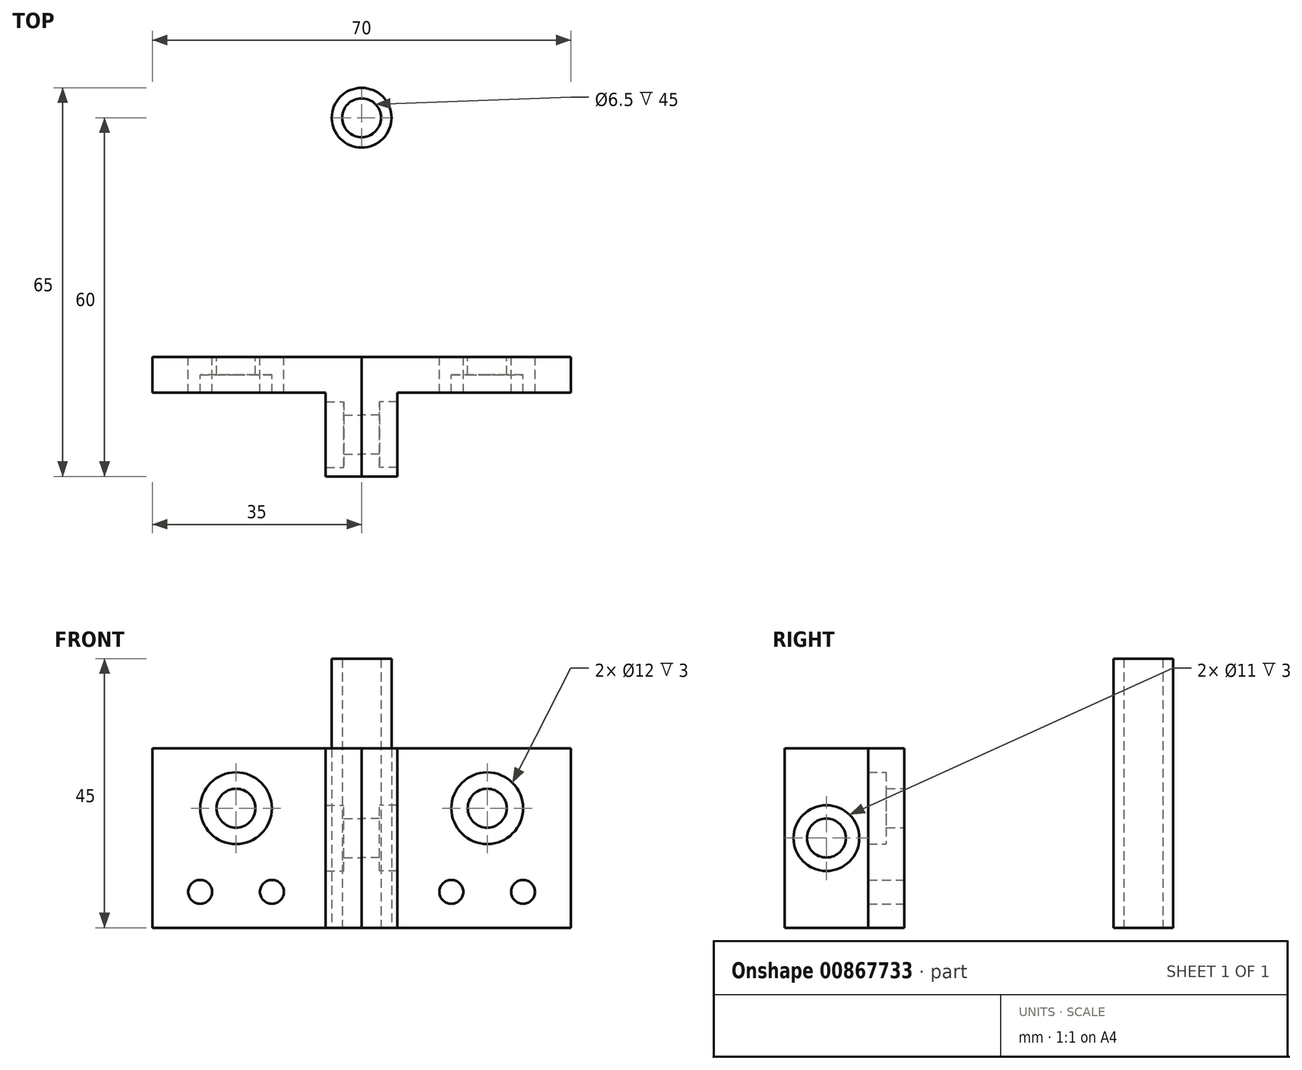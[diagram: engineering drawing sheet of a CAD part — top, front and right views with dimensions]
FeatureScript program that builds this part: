
annotation { "Feature Type Name" : "Feature", "Feature Type Description" : "" }
export const myFeature = defineFeature(function(context is Context, id is Id, definition is map)
    precondition{}
    {
        {
            var Q0;
            Q0=qCreatedBy(makeId("Top.planeOp"),FACE);
            var sketch = newSketch(context, id + "F0", { "sketchPlane" : qUnion([Q0])});
            skLineSegment(sketch, "E0", {"start": v(0, -20) * mm, "end": v(0, 0) * mm});
            skLineSegment(sketch, "E1", {"start": v(0, 0) * mm, "end": v(-35, 0) * mm});
            skLineSegment(sketch, "E2", {"start": v(-35, 0) * mm, "end": v(-35, -6) * mm});
            skLineSegment(sketch, "E3", {"start": v(-35, -6) * mm, "end": v(-6, -6) * mm});
            skLineSegment(sketch, "E4", {"start": v(-6, -6) * mm, "end": v(-6, -20) * mm});
            skLineSegment(sketch, "E5", {"start": v(-6, -20) * mm, "end": v(0, -20) * mm});
            skCircle(sketch, "E6", {"center": v(0, 40) * mm, "radius": 3.25 * mm});
            skCircle(sketch, "E7", {"center": v(0, 40) * mm, "radius": 5 * mm});
            skSolve(sketch);
        }
        {
            var Q0;
            Q0=makeQuery(id+"F0.imprint","IMPRINT",FACE,{"disambiguationData":[TD([[makeQuery(id+"F0.imprint","IMPRINT",EDGE,{"derivedFrom":sQuery(id+"F0.wireOp",EDGE,"E0")}),1.0]])]});
            extrude(context, id + "F1", {"entities" : qUnion([Q0]), "depth" : 30 * mm, "offsetDistance" : 25 * mm});
        }
        {
            var Q0;
            Q0=makeQuery(id+"F1.opExtrude","SWEPT_FACE",FACE,{"disambiguationData":[OSD([sQuery(id+"F0.wireOp",EDGE,"E3")])]});
            var sketch = newSketch(context, id + "F2", { "sketchPlane" : qUnion([Q0])});
            skLineSegment(sketch, "E8.0", {"start": v(-35, 30) * mm, "end": v(-35, 0) * mm, "construction": true});
            skPoint(sketch, "E9", {"position": v(-15, 6) * mm});
            skPoint(sketch, "E10", {"position": v(-21, 20) * mm});
            skPoint(sketch, "E11", {"position": v(-27, 6) * mm});
            skLineSegment(sketch, "E12.0", {"start": v(-35, 30) * mm, "end": v(-6, 30) * mm, "construction": true});
            skPoint(sketch, "E13.0", {"position": v(0, 30) * mm});
            skSolve(sketch);
        }
        {
            var Q0;
            Q0=sQuery(id+"F2.wireOp",VERTEX,"E10");
            var Q1;
            Q1=makeQuery(id+"F1.opExtrude","SWEPT_BODY",BODY,{"disambiguationData":[OSD([sQuery(id+"F0.wireOp",EDGE,"E0"),sQuery(id+"F0.wireOp",EDGE,"E1"),sQuery(id+"F0.wireOp",EDGE,"E2"),sQuery(id+"F0.wireOp",EDGE,"E3"),sQuery(id+"F0.wireOp",EDGE,"E4"),sQuery(id+"F0.wireOp",EDGE,"E5")])]});
            hole(context, id + "F3", {"style" : HoleStyle.C_BORE, "endStyle" : HoleEndStyle.THROUGH, "holeDiameter" : 6.5 * mm, "cBoreDiameter" : 12 * mm, "cBoreDepth" : 3 * mm, "majorDiameter" : 5 * mm, "isTappedThrough" : true, "tappedDepth" : 12 * mm, "tapClearance" : 3, "locations" : qUnion([Q0]), "scope" : qUnion([Q1])});
        }
        {
            var Q0;
            Q0=sQuery(id+"F2.wireOp",VERTEX,"E11");
            var Q1;
            Q1=sQuery(id+"F2.wireOp",VERTEX,"E9");
            var Q2;
            Q2=makeQuery(id+"F1.opExtrude","SWEPT_BODY",BODY,{"disambiguationData":[OSD([sQuery(id+"F0.wireOp",EDGE,"E0"),sQuery(id+"F0.wireOp",EDGE,"E1"),sQuery(id+"F0.wireOp",EDGE,"E2"),sQuery(id+"F0.wireOp",EDGE,"E3"),sQuery(id+"F0.wireOp",EDGE,"E4"),sQuery(id+"F0.wireOp",EDGE,"E5")])]});
            hole(context, id + "F4", {"style" : HoleStyle.SIMPLE, "endStyle" : HoleEndStyle.THROUGH, "holeDiameter" : 4 * mm, "majorDiameter" : 5 * mm, "isTappedThrough" : true, "tappedDepth" : 12 * mm, "tapClearance" : 3, "locations" : qUnion([Q0, Q1]), "scope" : qUnion([Q2])});
        }
        {
            var Q0;
            Q0=makeQuery(id+"F1.opExtrude","SWEPT_FACE",FACE,{"disambiguationData":[OSD([sQuery(id+"F0.wireOp",EDGE,"E4")])]});
            var sketch = newSketch(context, id + "F5", { "sketchPlane" : qUnion([Q0])});
            skLineSegment(sketch, "E14.0", {"start": v(20, 30) * mm, "end": v(20, 0) * mm, "construction": true});
            skLineSegment(sketch, "E15.0", {"start": v(6, 30) * mm, "end": v(20, 30) * mm, "construction": true});
            skPoint(sketch, "E16", {"position": v(13, 15) * mm});
            skPoint(sketch, "E16.positionSnap0", {"position": v(20, 15) * mm});
            skSolve(sketch);
        }
        {
            var Q0;
            Q0=sQuery(id+"F5.wireOp",VERTEX,"E16");
            var Q1;
            Q1=makeQuery(id+"F1.opExtrude","SWEPT_BODY",BODY,{"disambiguationData":[OSD([sQuery(id+"F0.wireOp",EDGE,"E0"),sQuery(id+"F0.wireOp",EDGE,"E1"),sQuery(id+"F0.wireOp",EDGE,"E2"),sQuery(id+"F0.wireOp",EDGE,"E3"),sQuery(id+"F0.wireOp",EDGE,"E4"),sQuery(id+"F0.wireOp",EDGE,"E5")])]});
            hole(context, id + "F6", {"style" : HoleStyle.C_BORE, "endStyle" : HoleEndStyle.THROUGH, "holeDiameter" : 6.5 * mm, "cBoreDiameter" : 11 * mm, "cBoreDepth" : 3 * mm, "majorDiameter" : 5 * mm, "isTappedThrough" : true, "tappedDepth" : 12 * mm, "tapClearance" : 3, "locations" : qUnion([Q0]), "scope" : qUnion([Q1])});
        }
        {
            var Q0;
            Q0=makeQuery(id+"F1.opExtrude","SWEPT_BODY",BODY,{"disambiguationData":[OSD([sQuery(id+"F0.wireOp",EDGE,"E0"),sQuery(id+"F0.wireOp",EDGE,"E1"),sQuery(id+"F0.wireOp",EDGE,"E2"),sQuery(id+"F0.wireOp",EDGE,"E3"),sQuery(id+"F0.wireOp",EDGE,"E4"),sQuery(id+"F0.wireOp",EDGE,"E5")])]});
            var Q1;
            Q1=qCreatedBy(makeId("Right.planeOp"),FACE);
            mirror(context, id + "F7", {"entities" : qUnion([Q0]), "mirrorPlane" : qUnion([Q1])});
        }
        {
            var Q0;
            Q0=makeQuery(id+"F0.imprint","IMPRINT",FACE,{"disambiguationData":[TD([[makeQuery(id+"F0.imprint","IMPRINT",EDGE,{"derivedFrom":sQuery(id+"F0.wireOp",EDGE,"E6")}),-1.0]])]});
            extrude(context, id + "F8", {"entities" : qUnion([Q0]), "depth" : 45 * mm, "offsetDistance" : 25 * mm});
        }
    });
